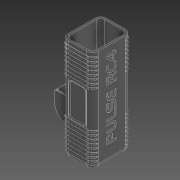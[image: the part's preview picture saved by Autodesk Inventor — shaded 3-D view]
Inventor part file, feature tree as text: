
AUTODESK INVENTOR PART (.ipt)
format: ipt  version: 2021 (Build 250183000, 183)  size: 2,434,560 bytes
history: native  units: mm
features: extrude x38, sketch x36, projected_geometry x24, fillet x18, plane x8, mirror x7, other x1
ambient origin geometry x8: Origin, YZ Plane, XZ Plane, XY Plane, X Axis, Y Axis, Z Axis, Center Point
bodies: Body1 (feature_tree)
feature tree (132):
  other  "Sólido1"
  extrude  "Extrusión1"  Depth=36.5mm
  extrude  "Extrusión2"  Depth=6.0mm
  extrude  "Extrusión3"  Depth=4.0mm
  plane  "Plano de trabajo1"
  mirror  "Simetría1"
  fillet  "Empalme1"  Radius=108.0mm
  plane  "Plano de trabajo2"
  extrude  "Extrusión4"  Depth=8.0mm
  plane  "Plano de trabajo3"
  mirror  "Simetría2"
  plane  "Plano de trabajo4"
  mirror  "Simetría3"
  plane  "Plano de trabajo5"
  mirror  "Simetría4"
  plane  "Plano de trabajo6"
  mirror  "Simetría5"
  plane  "Plano de trabajo8"
  mirror  "Simetría6"
  fillet  "Empalme2"  Radius=2.0mm
  fillet  "Empalme3"  Radius=2.0mm
  sketch  "Boceto4"  dims[d4=4.0mm d5=4.0mm d6=108.0mm d7=0.0mm]
  extrude  "Extrusión5"  Depth=2.0mm TaperAngle=0.0deg
  extrude  "Extrusión6"  Depth=6.0mm
  extrude  "Extrusión7"  Depth=11.0mm
  extrude  "Extrusión8"  [1 undecoded]
  extrude  "Extrusión9"  Depth=5.0mm
  extrude  "Extrusión10"  [1 undecoded]
  extrude  "Extrusión11"  [1 undecoded]
  extrude  "Extrusión12"  Depth=1.0mm
  extrude  "Extrusión13"  Depth=1.0mm TaperAngle=0.0deg
  extrude  "Extrusión14"  Depth=9.0mm
  extrude  "Extrusión15"  Depth=14.0mm TaperAngle=0.0deg
  extrude  "Extrusión16"  Depth=7.0mm
  fillet  "Empalme10"  Radius=1.8mm
  extrude  "Extrusión17"  Depth=2.0mm
  fillet  "Empalme13"  Radius=7.0mm
  fillet  "Empalme16"  Radius=6.0mm
  extrude  "Extrusión18"  Depth=8.0mm TaperAngle=0.0deg
  extrude  "Extrusión19"  Depth=8.0mm TaperAngle=0.0deg
  fillet  "Empalme31"  Radius=75.0mm
  fillet  "Empalme32"  Radius=75.0mm
  extrude  "Extrusión20"  Depth=11.273282mm
  extrude  "Extrusión21"  Depth=9.0mm
  extrude  "Extrusión22"  Depth=10.0mm TaperAngle=0.0deg
  extrude  "Extrusión23"  Depth=4.0mm
  mirror  "Simetría8"
  extrude  "Extrusión25"  Depth=2.0mm
  extrude  "Extrusión31"  Depth=0.5mm TaperAngle=0.0deg
  extrude  "Extrusión32"  Depth=0.5mm TaperAngle=0.0deg
  extrude  "Extrusión33"  Depth=4.0mm
  fillet  "Empalme39"  Radius=12.0mm
  extrude  "Extrusión34"  Depth=1.653837mm
  extrude  "Extrusión35"  Depth=10.0mm TaperAngle=0.0deg
  extrude  "Extrusión36"  Depth=1.0mm
  extrude  "Extrusión37"  Depth=10.0mm TaperAngle=0.0deg
  fillet  "Empalme41"  Radius=16.9mm
  fillet  "Empalme42"  Radius=10.0mm
  fillet  "Empalme43"  Radius=10.0mm
  fillet  "Empalme45"  Radius=9.0mm
  fillet  "Empalme46"  [1 undecoded]
  plane  "Plano de trabajo11"
  extrude  "Extrusión38"  Depth=10.0mm TaperAngle=0.0deg
  extrude  "Extrusión39"  Depth=10.0mm TaperAngle=0.0deg
  extrude  "Extrusión40"  Depth=1.0mm TaperAngle=0.0deg
  fillet  "Empalme47"  Radius=1.0mm
  extrude  "Extrusión41"  Depth=4.0mm TaperAngle=0.0deg
  fillet  "Empalme49"  Radius=2.0mm
  extrude  "Extrusión42"  Depth=1.0mm
  fillet  "Empalme50"  Radius=2.0mm
  extrude  "Extrusión43"  Depth=1.0mm
  extrude  "Extrusión44"  [1 undecoded]
  fillet  "Empalme51"  Radius=6.2mm
  sketch  "Boceto2"  dims[d0=27.85mm d1=36.5mm]
  sketch  "Boceto3"  dims[d2=2.0mm d3=6.0mm]
  sketch  "Boceto5"  dims[d8=2.0mm d9=0.0mm d10=8.0mm d11=2.0mm d12=2.0mm]
  sketch  "Boceto6"  dims[d13=2.0mm d14=2.0mm d15=0.0mm]
  sketch  "Boceto7"  dims[d16=20.0mm d17=6.0mm]
  sketch  "Boceto8"  dims[d18=3.2mm d19=11.0mm]
  projected_geometry  "Contorno proyectado1"
  sketch  "Boceto9"  dims[d20=5.0mm d21=-4.0mm]
  sketch  "Boceto10"  dims[d22=0.8mm d23=5.0mm]
  sketch  "Boceto11"  dims[d24=2.0mm d25=0.0mm d26=-3.0mm]
  sketch  "Boceto12"  dims[d27=-4.0mm d28=-8.0mm]
  sketch  "Boceto13"  dims[d29=-33.5mm d30=1.0mm]
  projected_geometry  "Contorno proyectado2"
  sketch  "Boceto14"  dims[d31=1.0mm d32=0.6mm d33=0.0mm]
  sketch  "Boceto18"  dims[d37=20.0mm d39=9.0mm]
  sketch  "Boceto19"  dims[d40=24.0mm d41=14.0mm d42=0.0mm]
  projected_geometry  "Contorno proyectado7"
  sketch  "Boceto20"  dims[d43=8.0mm d44=0.0mm d45=7.0mm d46=1.8mm]
  sketch  "Boceto21"  dims[d47=15.0mm d48=0.0mm d49=2.0mm d50=7.0mm d51=0.0mm d53=6.0mm d54=0.0mm]
  sketch  "Boceto22"  dims[d56=14.0mm d57=0.0mm d58=8.0mm d59=0.0mm]
  sketch  "Boceto24"  dims[d60=8.0mm d61=0.0mm d63=8.0mm d64=0.0mm d65=75.0mm d66=75.0mm]
  projected_geometry  "Contorno proyectado9"
  sketch  "Boceto25"  dims[d67=16.5mm d68=11.273282mm]
  sketch  "Boceto26"  dims[d70=5.0mm d72=9.0mm]
  projected_geometry  "Contorno proyectado10"
  projected_geometry  "Contorno proyectado11"
  projected_geometry  "Contorno proyectado12"
  projected_geometry  "Contorno proyectado13"
  sketch  "Boceto30"  dims[d73=9.0mm d75=10.0mm d76=0.0mm]
  projected_geometry  "Contorno proyectado16"
  sketch  "Boceto35"  dims[d78=6.0mm d79=4.0mm]
  projected_geometry  "Contorno proyectado21"
  sketch  "Boceto36"  dims[d80=6.0mm d81=2.0mm]
  projected_geometry  "Contorno proyectado22"
  projected_geometry  "Contorno proyectado23"
  sketch  "Boceto37"  dims[d82=2.0mm d83=0.5mm d84=0.0mm]
  projected_geometry  "Contorno proyectado24"
  sketch  "Boceto38"  dims[d85=2.0mm d88=0.5mm d89=0.0mm]
  projected_geometry  "Contorno proyectado25"
  sketch  "Boceto39"  dims[d90=1.5mm d93=4.0mm d96=12.0mm]
  projected_geometry  "Contorno proyectado26"
  sketch  "Boceto40"  dims[d97=1.5mm d98=1.653837mm]
  sketch  "Boceto41"  dims[d99=10.0mm d100=0.0mm d101=10.0mm d102=0.0mm]
  sketch  "Boceto42"  dims[d115=1.0mm d116=5.0mm]
  sketch  "Boceto43"  dims[d117=1.0mm d118=10.0mm d119=0.0mm d122=16.9mm d123=10.0mm d124=0.0mm d125=10.0mm d126=0.0mm d127=9.0mm d128=0.0mm d133=0.0mm d134=0.0mm]
  sketch  "Boceto44"  dims[d149=1.55mm d150=10.0mm d151=0.0mm]
  projected_geometry  "Contorno proyectado29"
  projected_geometry  "Contorno proyectado30"
  projected_geometry  "Contorno proyectado31"
  sketch  "Boceto45"  dims[d152=10.0mm d153=0.0mm d154=10.0mm d155=0.0mm]
  sketch  "Boceto46"  dims[d156=13.0mm d157=7.5mm d158=0.0mm d160=1.0mm d161=0.0mm]
  projected_geometry  "Contorno proyectado32"
  sketch  "Boceto47"  dims[d162=14.9mm d163=0.0mm d164=4.0mm d165=0.0mm d166=2.0mm]
  projected_geometry  "Contorno proyectado33"
  projected_geometry  "Contorno proyectado34"
  projected_geometry  "Contorno proyectado35"
  projected_geometry  "Contorno proyectado36"
  sketch  "Boceto48"  dims[d167=2.0mm d168=0.5mm d170=2.0mm d171=2.0mm d172=-13.0mm d173=6.2mm d174=4.0mm d175=0.0mm d176=4.0mm d177=0.0mm d178=4.0mm d179=0.0mm d180=2.0mm d181=3.0mm d182=2.0mm d183=0.0mm d185=1.0mm d186=26.0mm d187=0.0mm d188=1.0mm d189=10.0mm d190=0.0mm d191=1.0mm d192=0.0mm d193=1.0mm d74=0.5mm d77=0.872665mm d159=0.5mm]
  projected_geometry  "Contorno proyectado37"
note: 5 required parameter values undecoded (feature->parameter linkage not recoverable at this tier; creation-order binding heuristic only, values carry confidence <= 0.55)
